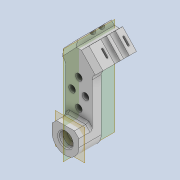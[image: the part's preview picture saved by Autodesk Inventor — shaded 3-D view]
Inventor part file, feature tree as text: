
AUTODESK INVENTOR PART (.ipt)
format: ipt  version: 2020 (Build 240168000, 168)  size: 408,064 bytes
history: native  units: mm
features: extrude x11, sketch x11, projected_geometry x8, thicken_offset x7, chamfer x4, fillet x4, other x4, plane x2, mirror x2, reference x2
ambient origin geometry x8: Origin, YZ Plane, XZ Plane, XY Plane, X Axis, Y Axis, Z Axis, Center Point
bodies: Solid1 (feature_tree)
feature tree (55):
  extrude  "Extrusion1"  Depth=30.0mm
  extrude  "Extrusion2"  Depth=10.0mm TaperAngle=0.0deg
  chamfer  "Chamfer1"  Distance=6.0mm
  extrude  "Extrusion3"  Depth=3.0mm TaperAngle=0.0deg
  extrude  "Extrusion4"  Depth=10.0mm
  extrude  "Extrusion5"  Depth=10.0mm
  thicken_offset  "Thicken1"
  thicken_offset  "Thicken2"
  extrude  "Extrusion6"  Depth=15.0mm TaperAngle=0.0deg
  extrude  "Extrusion7"  Depth=1.0mm
  chamfer  "Chamfer2"  Distance=2.5mm
  extrude  "Extrusion8"  Depth=15.0mm TaperAngle=0.0deg
  plane  "Work Plane2"
  mirror  "Mirror2"
  thicken_offset  "Thicken3"
  thicken_offset  "Thicken4"
  fillet  "Fillet2"  Radius=2.5mm
  fillet  "Fillet3"  Radius=15.0mm
  extrude  "Extrusion9"  Depth=1.0mm TaperAngle=45.0deg
  mirror  "Mirror3"
  fillet  "Fillet4"  Radius=15.0mm
  plane  "Work Plane3"
  extrude  "Extrusion10"  Depth=1.0mm
  chamfer  "Chamfer3"  Distance=1.0mm
  thicken_offset  "Thicken5"
  extrude  "Extrusion11"  Depth=1.0mm
  fillet  "Fillet5"  Radius=2.0mm
  chamfer  "Chamfer4"  Distance=3.0mm
  thicken_offset  "Thicken6"
  thicken_offset  "Thicken7"
  sketch  "Sketch1"  dims[d0=6.0mm d1=30.0mm]
  sketch  "Sketch2"  dims[d2=12.0mm d3=10.0mm d4=0.0mm]
  projected_geometry  "Projected Loop1"
  sketch  "Sketch3"  dims[d5=13.0mm]
  projected_geometry  "Projected Loop2"
  sketch  "Sketch4"  dims[d6=27.0mm d7=6.0mm d8=0.0mm]
  projected_geometry  "Projected Loop3"
  reference  "Reference1"
  sketch  "Sketch5"  dims[d9=3.0mm d10=2.0mm d11=45.0deg d12=6.0mm d13=0.0mm]
  projected_geometry  "Projected Loop4"
  sketch  "Sketch6"  dims[d14=10.0mm d15=4.0mm]
  sketch  "Sketch7"  dims[d16=10.0mm d17=4.0mm]
  sketch  "Sketch8"  dims[d18=15.0mm d19=0.0mm d20=15.0mm d21=0.0mm]
  reference  "Reference2"
  projected_geometry  "Projected Loop5"
  sketch  "Sketch9"  dims[d22=1.0mm d23=1.0mm]
  projected_geometry  "Projected Loop6"
  projected_geometry  "Projected Loop7"
  sketch  "Sketch10"  dims[d24=1.0mm]
  sketch  "Sketch11"  dims[d25=1.0mm d27=2.5mm d28=15.0mm d29=0.0mm d30=2.5mm d31=15.0mm d32=0.0mm d33=2.0mm d34=2.0mm d35=45.0deg d36=15.0mm d37=0.0mm d38=1.0mm d39=1.0mm d40=2.0mm d41=2.0mm d42=3.0mm d43=3.0mm d44=1.5mm d45=0.7mm d46=9.5mm d47=1.5mm d48=0.7mm d49=15.0mm d50=0.0mm d51=2.0mm d52=-2.0mm d53=1.0mm d54=6.0mm d55=0.0mm d56=1.0mm d57=2.0mm d58=45.0deg d59=1.0mm d60=1.0mm d61=5.0mm d62=6.0mm d63=12.0mm d64=3.0mm d65=3.0mm d66=3.0mm d67=3.0mm d68=3.0mm d69=3.0mm d70=3.0mm d71=6.0mm d72=0.0mm d73=1.0mm d74=0.5mm d75=2.0mm d76=45.0deg d77=0.05mm d78=0.05mm d79=0.05mm d80=0.05mm]
  projected_geometry  "Projected Loop8"
  parser-record x1  (decoder bookkeeping rows leaked as tree rows — omitted from the tree; the rows remain in map.json)
  other  "driver_ass_1.iam"
  other  "driver_wheel_1:1"
  other  "driver_wheel_1:2"
note: 1 file-system path scrubbed to <path> (originals preserved in map.json)
